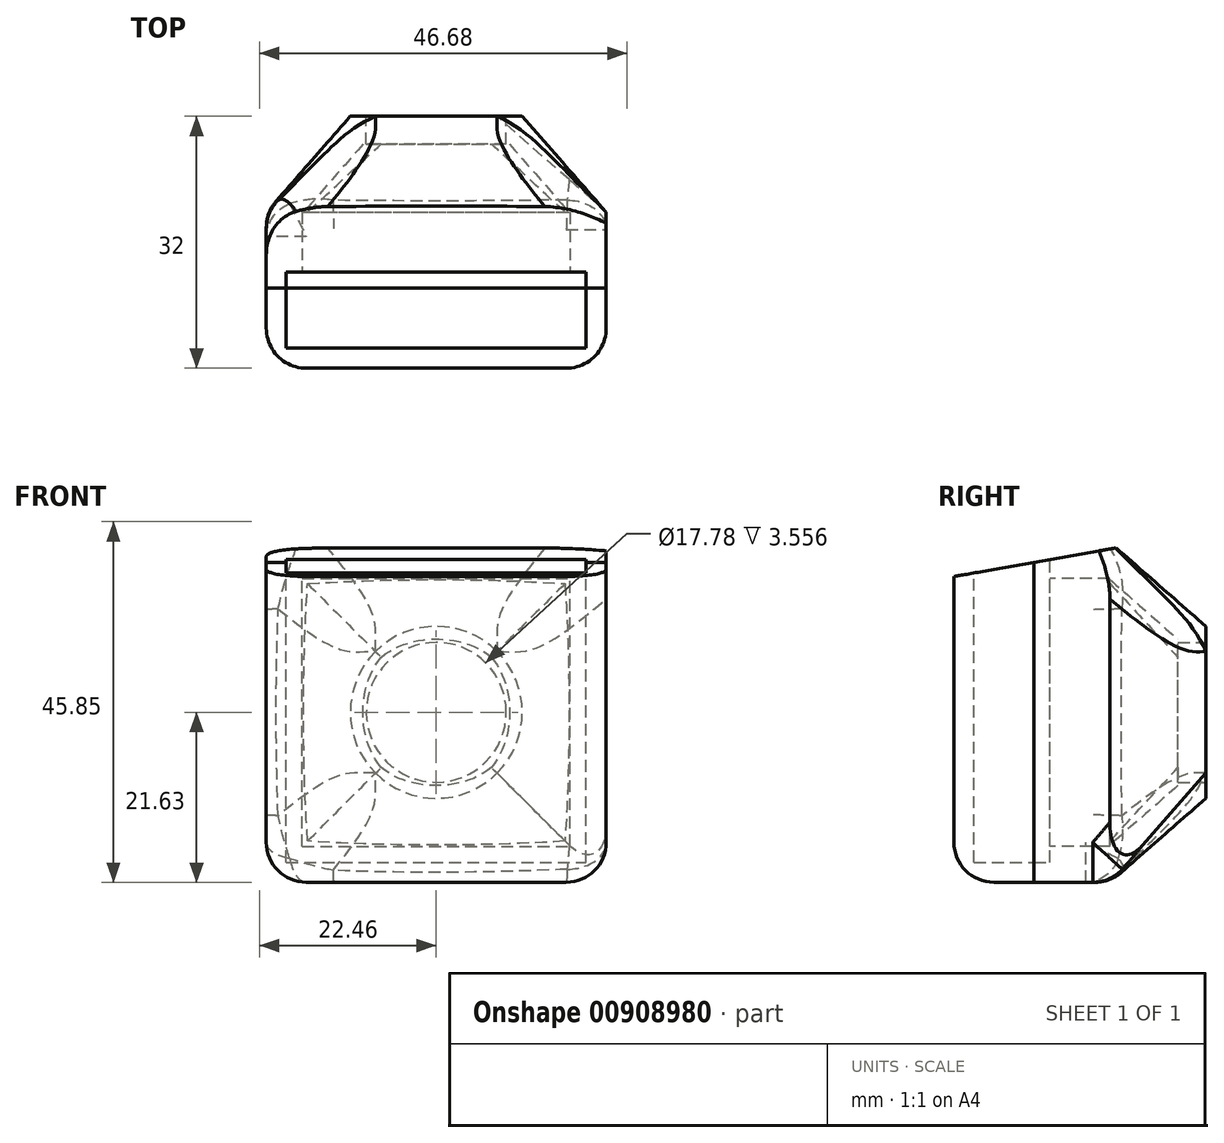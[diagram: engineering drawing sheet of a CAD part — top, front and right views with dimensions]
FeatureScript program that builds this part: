
annotation { "Feature Type Name" : "Feature", "Feature Type Description" : "" }
export const myFeature = defineFeature(function(context is Context, id is Id, definition is map)
    precondition{}
    {
        {
            var Q0;
            Q0=qCreatedBy(makeId("Front.planeOp"),FACE);
            var sketch = newSketch(context, id + "F0", { "sketchPlane" : qUnion([Q0])});
            skLineSegment(sketch, "E0.bottom", {"start": v(-19.05, -19.05) * mm, "end": v(19.05, -19.05) * mm});
            skLineSegment(sketch, "E0.top", {"start": v(-19.05, 19.05) * mm, "end": v(19.05, 19.05) * mm});
            skLineSegment(sketch, "E0.left", {"start": v(-19.05, -19.05) * mm, "end": v(-19.05, 19.05) * mm});
            skLineSegment(sketch, "E0.right", {"start": v(19.05, -19.05) * mm, "end": v(19.05, 19.05) * mm});
            skLineSegment(sketch, "E1.0", {"start": v(21.6, -21.59) * mm, "end": v(21.59, 21.6) * mm});
            skLineSegment(sketch, "E1.1", {"start": v(-21.59, -21.6) * mm, "end": v(21.6, -21.59) * mm});
            skLineSegment(sketch, "E1.2", {"start": v(-21.59, -21.6) * mm, "end": v(-21.6, 21.59) * mm});
            skLineSegment(sketch, "E2.0", {"start": v(17.02, -17.02) * mm, "end": v(17.02, 17.02) * mm});
            skLineSegment(sketch, "E2.1", {"start": v(-17.02, -17.02) * mm, "end": v(17.02, -17.02) * mm});
            skLineSegment(sketch, "E2.2", {"start": v(-17.02, -17.02) * mm, "end": v(-17.02, 17.02) * mm});
            skLineSegment(sketch, "E3.0", {"start": v(-21.6, 21.59) * mm, "end": v(21.59, 21.6) * mm});
            skLineSegment(sketch, "E4.0", {"start": v(-17.02, 17.02) * mm, "end": v(17.02, 17.02) * mm});
            skSolve(sketch);
        }
        {
            var Q0;
            Q0=makeQuery(id+"F0.imprint","IMPRINT",FACE,{"disambiguationData":[TD([[makeQuery(id+"F0.imprint","IMPRINT",EDGE,{"derivedFrom":sQuery(id+"F0.wireOp",EDGE,"E0.bottom")}),-1.0]])]});
            var Q1;
            Q1=makeQuery(id+"F0.imprint","IMPRINT",FACE,{"disambiguationData":[TD([[makeQuery(id+"F0.imprint","IMPRINT",EDGE,{"derivedFrom":sQuery(id+"F0.wireOp",EDGE,"E0.bottom")}),1.0]])]});
            extrude(context, id + "F1", {"entities" : qUnion([Q0, Q1]), "oppositeDirection" : true, "depth" : 7.62 * mm, "offsetDistance" : 25.4 * mm});
        }
        {
            var Q0;
            Q0 = qSketchRegion(id + "F0", true);
            extrude(context, id + "F2", {"entities" : qUnion([Q0]), "operationType" : NewBodyOperationType.ADD, "depth" : 2.03 * mm, "offsetDistance" : 25.4 * mm});
        }
        {
            var Q0;
            Q0=qCreatedBy(makeId("Front.planeOp"),FACE);
            cPlane(context, id + "F3", {"entities" : qUnion([Q0]), "cplaneType" : CPlaneType.OFFSET, "offset" : 19.8 * mm, "oppositeDirection" : true, "width" : 152.4 * mm, "height" : 152.4 * mm});
        }
        {
            var Q0;
            Q0=qCreatedBy(id+"F3.planeOp",FACE);
            var sketch = newSketch(context, id + "F4", { "sketchPlane" : qUnion([Q0])});
            skCircle(sketch, "E5", {"center": v(0, 0) * mm, "radius": 8.9 * mm, "construction": true});
            skCircle(sketch, "E6.0", {"center": v(0, 0) * mm, "radius": 10.92 * mm});
            skSolve(sketch);
        }
        {
            var Q0;
            Q0=qCreatedBy(makeId("Front.planeOp"),FACE);
            cPlane(context, id + "F5", {"entities" : qUnion([Q0]), "cplaneType" : CPlaneType.OFFSET, "offset" : 7.62 * mm, "oppositeDirection" : true, "width" : 152.4 * mm, "height" : 152.4 * mm});
        }
        {
            var Q0;
            Q0=qCreatedBy(id+"F5.planeOp",FACE);
            var sketch = newSketch(context, id + "F6", { "sketchPlane" : qUnion([Q0])});
            skLineSegment(sketch, "E7.bottom", {"start": v(21.59, 21.6) * mm, "end": v(-21.59, 21.6) * mm});
            skLineSegment(sketch, "E7.top", {"start": v(21.59, -21.59) * mm, "end": v(-21.59, -21.59) * mm});
            skLineSegment(sketch, "E7.left", {"start": v(21.59, 21.6) * mm, "end": v(21.59, -21.59) * mm});
            skLineSegment(sketch, "E7.right", {"start": v(-21.59, 21.6) * mm, "end": v(-21.59, -21.59) * mm});
            skSolve(sketch);
        }
        {
            var Q0;
            Q0=makeQuery(id+"F6.imprint","IMPRINT",FACE,{"disambiguationData":[TD([[makeQuery(id+"F6.imprint","IMPRINT",EDGE,{"derivedFrom":sQuery(id+"F6.wireOp",EDGE,"E7.bottom")}),1.0]])]});
            var Q1;
            Q1=makeQuery(id+"F4.imprint","IMPRINT",FACE,{"disambiguationData":[TD([[makeQuery(id+"F4.imprint","IMPRINT",EDGE,{"derivedFrom":sQuery(id+"F4.wireOp",EDGE,"E6.0")}),1.0]])]});
            loft(context, id + "F7", {"sheetProfilesArray" : [{ "sheetProfileEntities" : qUnion([Q0]) }, { "sheetProfileEntities" : qUnion([Q1]) }]});
        }
        {
            var Q0;
            Q0=makeQuery(id+"F7.opLoft","CAP_FACE",FACE,{"disambiguationData":[OSD([makeQuery(id+"F6.imprint","IMPRINT",FACE,{"disambiguationData":[TD([[makeQuery(id+"F6.imprint","IMPRINT",EDGE,{"derivedFrom":sQuery(id+"F6.wireOp",EDGE,"E7.bottom")}),1.0]])]})])],"isStart":true});
            shell(context, id + "F8", {"entities" : qUnion([Q0]), "thickness" : 3.56 * mm});
        }
        {
            var Q0;
            Q0=qCreatedBy(id+"F3.planeOp",FACE);
            var sketch = newSketch(context, id + "F9", { "sketchPlane" : qUnion([Q0])});
            skCircle(sketch, "E8", {"center": v(0, 0) * mm, "radius": 8.9 * mm});
            skSolve(sketch);
        }
        {
            var Q0;
            Q0=makeQuery(id+"F1.opExtrude","SWEPT_BODY",BODY,{"disambiguationData":[OSD([sQuery(id+"F0.wireOp",EDGE,"E1.0"),sQuery(id+"F0.wireOp",EDGE,"E1.1"),sQuery(id+"F0.wireOp",EDGE,"E1.2"),sQuery(id+"F0.wireOp",EDGE,"E2.0"),sQuery(id+"F0.wireOp",EDGE,"E2.1"),sQuery(id+"F0.wireOp",EDGE,"E2.2"),sQuery(id+"F0.wireOp",EDGE,"E3.0"),sQuery(id+"F0.wireOp",EDGE,"E4.0")])]});
            var Q1;
            Q1=makeQuery(id+"F7.opLoft","SWEPT_BODY",BODY,{"disambiguationData":[OSD([makeQuery(id+"F4.imprint","IMPRINT",FACE,{"disambiguationData":[TD([[makeQuery(id+"F4.imprint","IMPRINT",EDGE,{"derivedFrom":sQuery(id+"F4.wireOp",EDGE,"E6.0")}),1.0]])]}),makeQuery(id+"F6.imprint","IMPRINT",FACE,{"disambiguationData":[TD([[makeQuery(id+"F6.imprint","IMPRINT",EDGE,{"derivedFrom":sQuery(id+"F6.wireOp",EDGE,"E7.bottom")}),1.0]])]})])]});
            booleanBodies(context, id + "F10", {"operationType" : BooleanOperationType.UNION, "tools" : qUnion([Q0, Q1])});
        }
        {
            var Q0;
            Q0 = qSketchRegion(id + "F9", true);
            extrude(context, id + "F11", {"entities" : qUnion([Q0]), "operationType" : NewBodyOperationType.REMOVE, "depth" : 25.4 * mm, "offsetDistance" : 25.4 * mm});
        }
        {
            var Q0;
            Q0=makeQuery(id+"F7.opLoft","SWEPT_EDGE",EDGE,{"disambiguationData":[OSD([sQuery(id+"F4.wireOp",EDGE,"E6.0"),sQuery(id+"F6.wireOp",EDGE,"E7.bottom"),sQuery(id+"F6.wireOp",EDGE,"E7.top"),sQuery(id+"F6.wireOp",EDGE,"E7.right")])]});
            var Q1;
            Q1=makeQuery(id+"F7.opLoft","SWEPT_EDGE",EDGE,{"disambiguationData":[OSD([sQuery(id+"F6.wireOp",EDGE,"E7.bottom"),sQuery(id+"F6.wireOp",EDGE,"E7.left")])]});
            var Q2;
            Q2=makeQuery(id+"F7.opLoft","SWEPT_EDGE",EDGE,{"disambiguationData":[OSD([sQuery(id+"F4.wireOp",EDGE,"E6.0"),sQuery(id+"F6.wireOp",EDGE,"E7.bottom"),sQuery(id+"F6.wireOp",EDGE,"E7.top"),sQuery(id+"F6.wireOp",EDGE,"E7.left")])]});
            var Q3;
            Q3=makeQuery(id+"F7.opLoft","SWEPT_EDGE",EDGE,{"disambiguationData":[OSD([sQuery(id+"F4.wireOp",EDGE,"E6.0"),sQuery(id+"F6.wireOp",EDGE,"E7.top"),sQuery(id+"F6.wireOp",EDGE,"E7.left"),sQuery(id+"F6.wireOp",EDGE,"E7.right")])]});
            fillet(context, id + "F12", {"entities" : qUnion([Q0, Q1, Q2, Q3]), "radius" : 10.16 * mm, "tangentPropagation" : true, "allowEdgeOverflow" : false});
        }
        {
            var Q0;
            {var subQ0=sQuery(id+"F0.wireOp",EDGE,"E1.2");var subQ1=sQuery(id+"F0.wireOp",EDGE,"E1.1");Q0=makeQuery(id+"F2.boolean.opBoolean","MERGE",EDGE,{"derivedFrom":[makeQuery(id+"F1.opExtrude","SWEPT_EDGE",EDGE,{"disambiguationData":[OSD([subQ1,subQ0])]}),makeQuery(id+"F2.opExtrude","SWEPT_EDGE",EDGE,{"disambiguationData":[OSD([subQ1,subQ0])]})]});}
            var Q1;
            {var subQ0=sQuery(id+"F0.wireOp",EDGE,"E1.1");var subQ1=sQuery(id+"F0.wireOp",EDGE,"E1.0");Q1=makeQuery(id+"F2.boolean.opBoolean","MERGE",EDGE,{"derivedFrom":[makeQuery(id+"F1.opExtrude","SWEPT_EDGE",EDGE,{"disambiguationData":[OSD([subQ1,subQ0])]}),makeQuery(id+"F2.opExtrude","SWEPT_EDGE",EDGE,{"disambiguationData":[OSD([subQ1,subQ0])]})]});}
            fillet(context, id + "F13", {"entities" : qUnion([Q0, Q1]), "radius" : 5.08 * mm, "tangentPropagation" : true, "allowEdgeOverflow" : false});
        }
        {
            var Q0;
            Q0=makeQuery(id+"F10.opBoolean","MERGE",EDGE,{"derivedFrom":[makeQuery(id+"F1.opExtrude","CAP_EDGE",EDGE,{"disambiguationData":[OSD([sQuery(id+"F0.wireOp",EDGE,"E1.1")])],"isStart":false}),makeQuery(id+"F7.opLoft","MID_CAP_EDGE",EDGE,{"disambiguationData":[OSD([sQuery(id+"F6.wireOp",EDGE,"E7.top"),sQuery(id+"F6.wireOp",EDGE,"E7.left"),sQuery(id+"F6.wireOp",EDGE,"E7.right")])],"capPos":0.0})]});
            fillet(context, id + "F14", {"entities" : qUnion([Q0]), "radius" : 5.08 * mm, "tangentPropagation" : true, "allowEdgeOverflow" : false});
        }
        {
            var Q0;
            Q0=makeQuery(id+"F2.opExtrude","CAP_FACE",FACE,{"disambiguationData":[OSD([sQuery(id+"F0.wireOp",EDGE,"E0.bottom"),sQuery(id+"F0.wireOp",EDGE,"E0.top"),sQuery(id+"F0.wireOp",EDGE,"E0.left"),sQuery(id+"F0.wireOp",EDGE,"E0.right"),sQuery(id+"F0.wireOp",EDGE,"E1.0"),sQuery(id+"F0.wireOp",EDGE,"E1.1"),sQuery(id+"F0.wireOp",EDGE,"E1.2"),sQuery(id+"F0.wireOp",EDGE,"E3.0")])],"isStart":false});
            cPlane(context, id + "F15", {"entities" : qUnion([Q0]), "cplaneType" : CPlaneType.OFFSET, "offset" : 0 * mm, "width" : 152.4 * mm, "height" : 152.4 * mm});
        }
        {
            var Q0;
            Q0=qCreatedBy(id+"F15.planeOp",FACE);
            var sketch = newSketch(context, id + "F16", { "sketchPlane" : qUnion([Q0])});
            skLineSegment(sketch, "E9.0.0", {"start": v(-16.5, -21.6) * mm, "end": v(16.51, -21.59) * mm});
            skArc(sketch, "E9.0.1", {"start": v(16.51, -21.59) * mm, "mid": v(20.1, -20.1) * mm, "end": v(21.6, -16.5) * mm});
            skLineSegment(sketch, "E9.0.2", {"start": v(21.6, -16.5) * mm, "end": v(21.59, 21.6) * mm});
            skLineSegment(sketch, "E9.0.3", {"start": v(21.59, 21.6) * mm, "end": v(-21.6, 21.59) * mm});
            skLineSegment(sketch, "E9.0.4", {"start": v(-21.6, 21.59) * mm, "end": v(-21.59, -16.51) * mm});
            skArc(sketch, "E9.0.5", {"start": v(-21.59, -16.51) * mm, "mid": v(-20.1, -20.1) * mm, "end": v(-16.5, -21.6) * mm});
            skLineSegment(sketch, "E10.0", {"start": v(-19.05, 19.05) * mm, "end": v(19.05, 19.05) * mm});
            skLineSegment(sketch, "E10.1", {"start": v(-19.05, -19.05) * mm, "end": v(-19.05, 19.05) * mm});
            skLineSegment(sketch, "E10.2", {"start": v(19.05, -19.05) * mm, "end": v(19.05, 19.05) * mm});
            skLineSegment(sketch, "E10.3", {"start": v(-19.05, -19.05) * mm, "end": v(19.05, -19.05) * mm});
            skSolve(sketch);
        }
        {
            var Q0;
            Q0 = qSketchRegion(id + "F16", true);
            var Q1;
            Q1=makeQuery(id+"F16.imprint","IMPRINT",FACE,{"disambiguationData":[TD([[makeQuery(id+"F16.imprint","IMPRINT",EDGE,{"derivedFrom":sQuery(id+"F16.wireOp",EDGE,"E10.0")}),-1.0]])]});
            extrude(context, id + "F17", {"entities" : qUnion([Q0, Q1]), "depth" : 10.16 * mm, "offsetDistance" : 25.4 * mm});
        }
        {
            var Q0;
            Q0=makeQuery(id+"F16.imprint","IMPRINT",FACE,{"disambiguationData":[TD([[makeQuery(id+"F16.imprint","IMPRINT",EDGE,{"derivedFrom":sQuery(id+"F16.wireOp",EDGE,"E10.0")}),-1.0]])]});
            extrude(context, id + "F18", {"entities" : qUnion([Q0]), "operationType" : NewBodyOperationType.REMOVE, "depth" : 7.62 * mm, "offsetDistance" : 25.4 * mm});
        }
        {
            var Q0;
            Q0=makeQuery(id+"F17.opExtrude","CAP_EDGE",EDGE,{"disambiguationData":[OSD([sQuery(id+"F16.wireOp",EDGE,"E9.0.4")])],"isStart":false});
            fillet(context, id + "F19", {"entities" : qUnion([Q0]), "radius" : 5.08 * mm, "tangentPropagation" : true, "allowEdgeOverflow" : false});
        }
        {
            var Q0;
            Q0=qCreatedBy(makeId("Right.planeOp"),FACE);
            var sketch = newSketch(context, id + "F20", { "sketchPlane" : qUnion([Q0])});
            skLineSegment(sketch, "E11.0", {"start": v(-35.8, 21.59) * mm, "end": v(7.65, 21.59) * mm, "construction": true});
            skPoint(sketch, "E11.1", {"position": v(-4.57, 21.59) * mm});
            skPoint(sketch, "E12.orphan", {"position": v(-7.11, 21.59) * mm});
            skPoint(sketch, "E13.orphan", {"position": v(-2.03, 21.59) * mm});
            skLineSegment(sketch, "E14.0", {"start": v(-2.03, 19.05) * mm, "end": v(0, 19.05) * mm, "construction": true});
            skLineSegment(sketch, "E15", {"start": v(17.06, 22.42) * mm, "end": v(-40.64, 12.24) * mm});
            skLineSegment(sketch, "E16", {"start": v(17.06, 22.42) * mm, "end": v(9.86, 32.6) * mm});
            skLineSegment(sketch, "E17", {"start": v(9.86, 32.6) * mm, "end": v(-32.47, 28.32) * mm});
            skLineSegment(sketch, "E18", {"start": v(-32.47, 28.32) * mm, "end": v(-40.64, 12.24) * mm});
            skSolve(sketch);
        }
        {
            var Q0;
            Q0 = qSketchRegion(id + "F20", true);
            extrude(context, id + "F21", {"entities" : qUnion([Q0]), "operationType" : NewBodyOperationType.REMOVE, "endBound" : BoundingType.SYMMETRIC, "depth" : 75.49 * mm, "offsetDistance" : 25.4 * mm});
        }
        {
            var Q0;
            Q0=qCreatedBy(id+"F15.planeOp",FACE);
            var sketch = newSketch(context, id + "F22", { "sketchPlane" : qUnion([Q0])});
            skLineSegment(sketch, "E19.0", {"start": v(-19.05, -19.05) * mm, "end": v(-19.05, 19.05) * mm});
            skLineSegment(sketch, "E19.1", {"start": v(19.05, -19.05) * mm, "end": v(19.05, 19.05) * mm});
            skLineSegment(sketch, "E20.bottom", {"start": v(-19.05, 19.05) * mm, "end": v(19.05, 19.05) * mm});
            skLineSegment(sketch, "E20.top", {"start": v(-19.05, 24.28) * mm, "end": v(19.05, 24.28) * mm});
            skLineSegment(sketch, "E20.left", {"start": v(-19.05, 19.05) * mm, "end": v(-19.05, 24.28) * mm});
            skLineSegment(sketch, "E20.right", {"start": v(19.05, 19.05) * mm, "end": v(19.05, 24.28) * mm});
            skSolve(sketch);
        }
        {
            var Q0;
            Q0=makeQuery(id+"F22.imprint","IMPRINT",FACE,{"disambiguationData":[TD([[makeQuery(id+"F22.imprint","IMPRINT",EDGE,{"derivedFrom":sQuery(id+"F22.wireOp",EDGE,"E20.bottom")}),1.0]])]});
            extrude(context, id + "F23", {"entities" : qUnion([Q0]), "operationType" : NewBodyOperationType.REMOVE, "oppositeDirection" : true, "depth" : 2.03 * mm, "offsetDistance" : 25.4 * mm});
        }
    });
